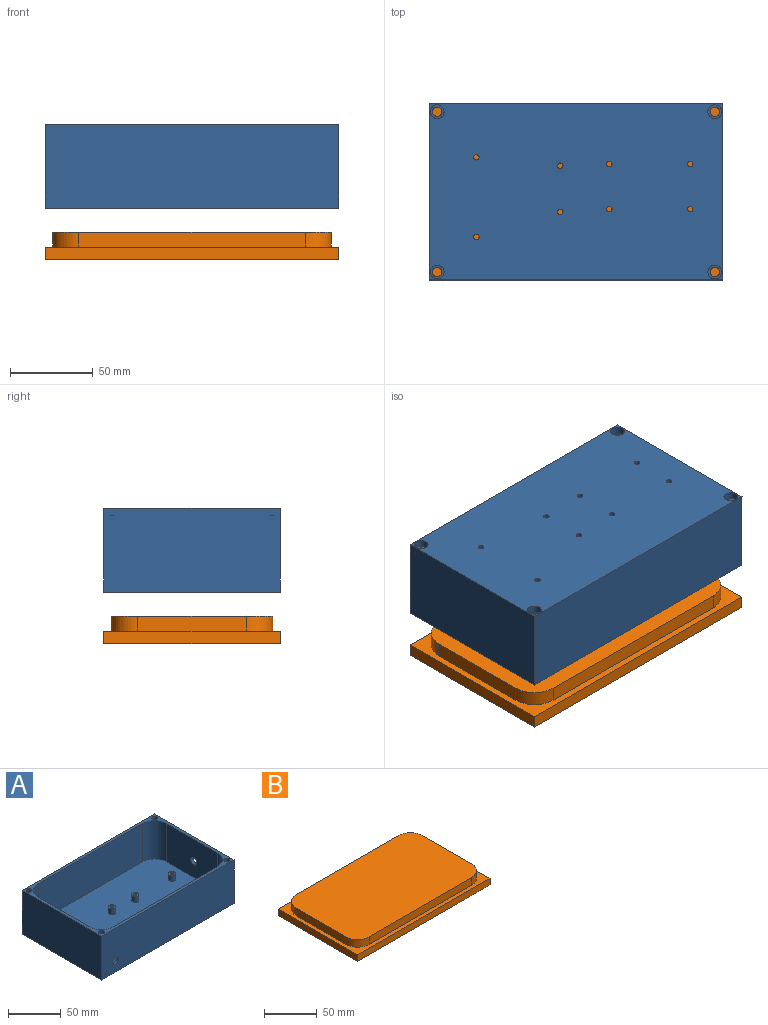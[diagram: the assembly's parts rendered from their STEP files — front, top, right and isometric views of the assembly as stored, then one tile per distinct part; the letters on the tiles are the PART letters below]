
ASSEMBLY  parts=2 mates=2
PART A: 53 faces, bbox 177.8x106.7x50.8 mm
  f0: cylinder r=15.88mm len=44.45mm, axis (0,0,1), area 1083.9mm2, adj f5,f7,f8,f14,f35
  f1: plane 106.68x50.8mm, normal (-1,0,0), area 5419.3mm2, adj f2,f4,f5,f6
  f2: plane 177.8x50.8mm, normal (0,-1,0), area 8983.5mm2, adj f1,f3,f5,f6,f35
  f3: plane 106.68x50.8mm, normal (1,0,0), area 5367.5mm2, adj f2,f4,f5,f6,f36
  f4: plane 177.8x50.8mm, normal (0,1,0), area 9032.2mm2, adj f1,f3,f5,f6
  f5: plane 177.8x106.68mm, normal (0,0,1), area 1879.8mm2, adj f0,f1,f2,f3,f4,f7,f8,f9
  f6: plane 177.8x106.68mm, normal (0,0,-1), area 18678.5mm2, adj f1,f2,f3,f4,f17,f20,f23,f26
  f7: plane 68.58x44.45mm, normal (1,0,0), area 3048.4mm2, adj f0,f5,f13,f14
  f8: plane 139.7x44.45mm, normal (0,1,0), area 6185.3mm2, adj f0,f5,f9,f14,f35
  f9: cylinder r=15.88mm len=44.45mm, axis (0,0,1), area 1108.4mm2, adj f5,f8,f10,f14
  f10: plane 68.58x44.45mm, normal (-1,0,0), area 2996.5mm2, adj f5,f9,f11,f14,f36
  f11: cylinder r=15.88mm len=44.45mm, axis (0,0,1), area 1108.4mm2, adj f5,f10,f12,f14
  f12: plane 139.7x44.45mm, normal (0,-1,0), area 6209.7mm2, adj f5,f11,f13,f14
  f13: cylinder r=15.88mm len=44.45mm, axis (0,0,1), area 1108.4mm2, adj f5,f7,f12,f14
  f14: plane 171.45x100.33mm, normal (0,0,1), area 16678.7mm2, adj f0,f7,f8,f9,f10,f11,f12,f13
  f15: cylinder r=2.86mm len=46.36mm, axis (0,0,-1), area 832.3mm2, adj f5,f16
  f16: plane 8.38x8.38mm, normal (0,0,-1), area 29.5mm2, adj f15,f17
  f17: cylinder r=4.19mm len=8.38mm, axis (0,0,-1), area 117mm2, adj f6,f16
  f18: cylinder r=2.86mm len=46.36mm, axis (0,0,-1), area 832.3mm2, adj f5,f19
  f19: plane 8.38x8.38mm, normal (0,0,-1), area 29.5mm2, adj f18,f20
  f20: cylinder r=4.19mm len=8.38mm, axis (0,0,-1), area 117mm2, adj f6,f19
  f21: cylinder r=2.86mm len=46.36mm, axis (0,0,-1), area 832.3mm2, adj f5,f22
  f22: plane 8.38x8.38mm, normal (0,0,-1), area 29.5mm2, adj f21,f23
  f23: cylinder r=4.19mm len=8.38mm, axis (0,0,-1), area 117mm2, adj f6,f22
  f24: cylinder r=2.86mm len=46.36mm, axis (0,0,-1), area 832.3mm2, adj f5,f25
  f25: plane 8.38x8.38mm, normal (0,0,-1), area 29.5mm2, adj f24,f26
  f26: cylinder r=4.19mm len=8.38mm, axis (0,0,-1), area 117mm2, adj f6,f25
  f27: cylinder r=1.65mm len=12.7mm, axis (0,0,1), area 131.7mm2, adj f6,f40
  f28: cylinder r=1.65mm len=12.7mm, axis (0,0,1), area 131.7mm2, adj f6,f42
  f29: cylinder r=1.65mm len=12.7mm, axis (0,0,1), area 131.7mm2, adj f6,f44
  f30: cylinder r=1.65mm len=12.7mm, axis (0,0,1), area 131.7mm2, adj f6,f38
  f31: cylinder r=1.65mm len=12.7mm, axis (0,0,1), area 131.7mm2, adj f6,f50
  f32: cylinder r=1.65mm len=12.7mm, axis (0,0,1), area 131.7mm2, adj f6,f52
  f33: cylinder r=1.65mm len=12.7mm, axis (0,0,1), area 131.7mm2, adj f6,f46
  f34: cylinder r=1.65mm len=12.7mm, axis (0,0,1), area 131.7mm2, adj f6,f48
  f35: cylinder r=3.94mm len=7.87mm, axis (0,-1,0), area 81.6mm2, adj f0,f2,f8
  f36: cylinder r=4.06mm len=8.13mm, axis (1,0,0), area 81.1mm2, adj f3,f10
  f37: cylinder r=3.49mm len=6.99mm, axis (0,0,-1), area 139.3mm2, adj f14,f38
  f38: plane 6.99x6.99mm, normal (0,0,1), area 29.8mm2, adj f30,f37
  f39: cylinder r=3.49mm len=6.99mm, axis (0,0,-1), area 139.3mm2, adj f14,f40
  f40: plane 6.99x6.99mm, normal (0,0,1), area 29.8mm2, adj f27,f39
  f41: cylinder r=3.49mm len=6.99mm, axis (0,0,-1), area 139.3mm2, adj f14,f42
  f42: plane 6.99x6.99mm, normal (0,0,1), area 29.8mm2, adj f28,f41
  f43: cylinder r=3.49mm len=6.99mm, axis (0,0,-1), area 139.3mm2, adj f14,f44
  f44: plane 6.99x6.99mm, normal (0,0,1), area 29.8mm2, adj f29,f43
  f45: cylinder r=3.49mm len=6.99mm, axis (0,0,-1), area 139.3mm2, adj f14,f46
  f46: plane 6.99x6.99mm, normal (0,0,1), area 29.8mm2, adj f33,f45
  f47: cylinder r=3.49mm len=6.99mm, axis (0,0,-1), area 139.3mm2, adj f14,f48
  f48: plane 6.99x6.99mm, normal (0,0,1), area 29.8mm2, adj f34,f47
  f49: cylinder r=3.49mm len=6.99mm, axis (0,0,-1), area 139.3mm2, adj f14,f50
  f50: plane 6.99x6.99mm, normal (0,0,1), area 29.8mm2, adj f31,f49
  f51: cylinder r=3.49mm len=6.99mm, axis (0,0,-1), area 139.3mm2, adj f14,f52
  f52: plane 6.99x6.99mm, normal (0,0,1), area 29.8mm2, adj f32,f51
PART B: 15 faces, bbox 177.8x106.7x16.5 mm
  f0: plane 106.68x7.62mm, normal (-1,0,0), area 812.9mm2, adj f1,f3,f4,f13
  f1: plane 177.8x7.62mm, normal (0,-1,0), area 1354.8mm2, adj f0,f2,f4,f13
  f2: plane 106.68x7.62mm, normal (1,0,0), area 812.9mm2, adj f1,f3,f4,f13
  f3: plane 177.8x7.62mm, normal (0,1,0), area 1354.8mm2, adj f0,f2,f4,f13
  f4: plane 177.8x106.68mm, normal (0,0,-1), area 18967.7mm2, adj f0,f1,f2,f3
  f5: cylinder r=15.88mm len=15.88mm, axis (0,0,1), area 221.7mm2, adj f6,f12,f13,f14
  f6: plane 66.04x8.89mm, normal (-1,0,0), area 587.1mm2, adj f5,f7,f13,f14
  f7: cylinder r=15.88mm len=15.88mm, axis (0,0,1), area 221.7mm2, adj f6,f8,f13,f14
  f8: plane 137.16x8.89mm, normal (0,1,0), area 1219.4mm2, adj f7,f9,f13,f14
  f9: cylinder r=15.88mm len=15.88mm, axis (0,0,1), area 221.7mm2, adj f8,f10,f13,f14
  f10: plane 66.04x8.89mm, normal (1,0,0), area 587.1mm2, adj f9,f11,f13,f14
  f11: cylinder r=15.88mm len=15.88mm, axis (0,0,1), area 221.7mm2, adj f10,f12,f13,f14
  f12: plane 137.16x8.89mm, normal (0,-1,0), area 1219.4mm2, adj f5,f11,f13,f14
  f13: plane 177.8x106.68mm, normal (0,0,1), area 2666.3mm2, adj f0,f1,f2,f3,f5,f6,f7,f8
  f14: plane 168.91x97.79mm, normal (0,0,1), area 16301.4mm2, adj f5,f6,f7,f8,f9,f10,f11,f12
PLACE A rot(axis=(-1,0,0),180deg) t=(167.82,60.48,-8.61)mm
PLACE B t=(167.82,-46.2,-90.66)mm
MATE planar B.f1 <-> A.f4  axis (0,-1,0) through (256.72,-46.2,-86.85)mm
MATE planar B.f2 <-> A.f3  axis (1,0,0) through (345.62,7.14,-86.85)mm
